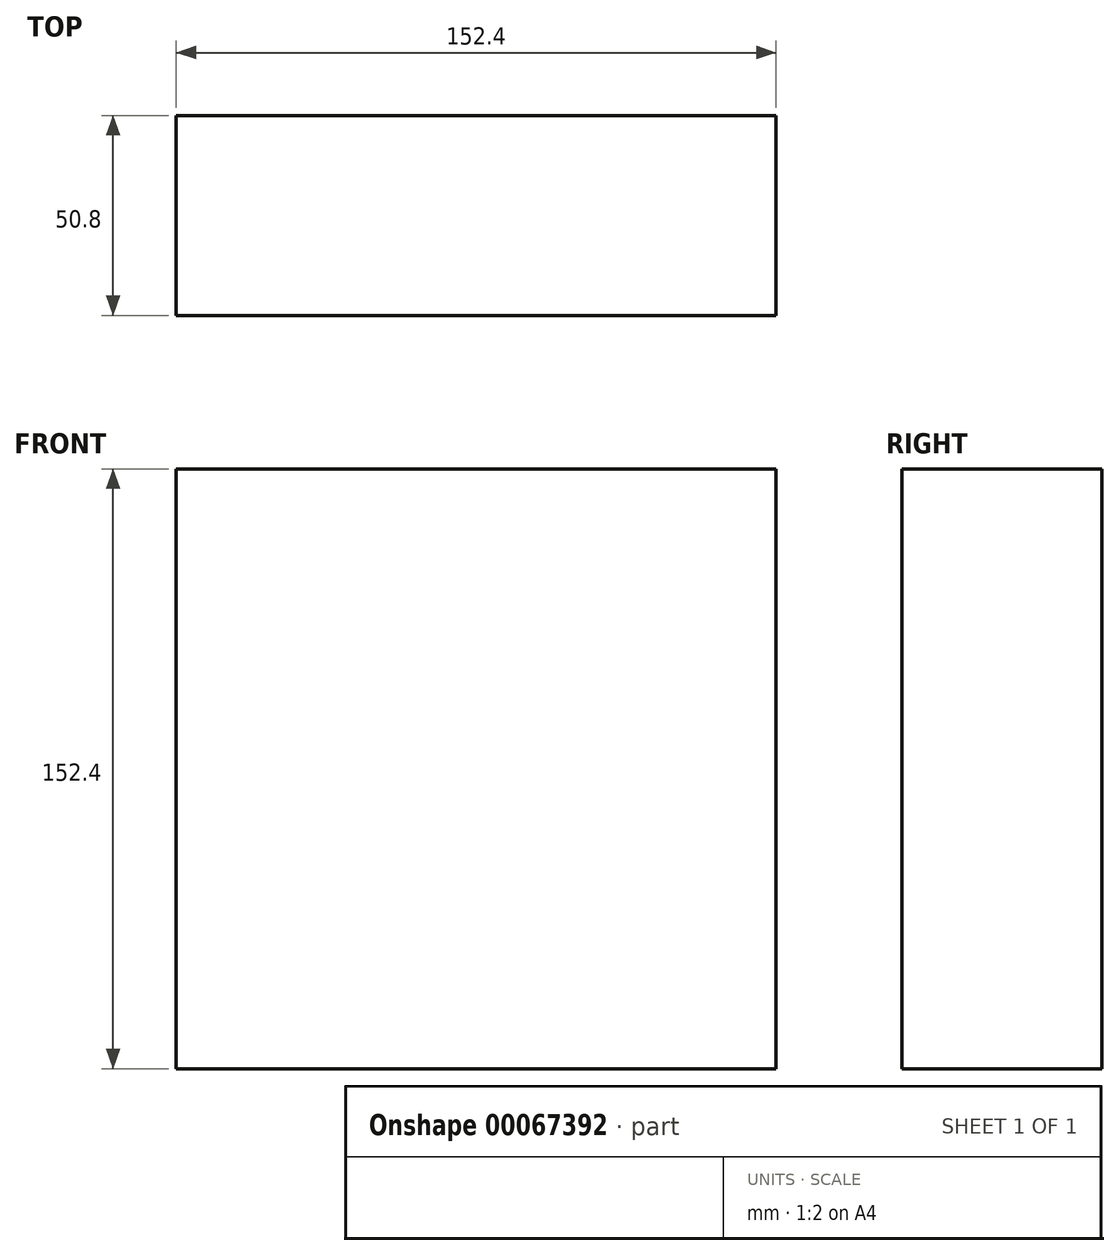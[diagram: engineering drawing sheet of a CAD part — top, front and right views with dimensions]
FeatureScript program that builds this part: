
annotation { "Feature Type Name" : "Feature", "Feature Type Description" : "" }
export const myFeature = defineFeature(function(context is Context, id is Id, definition is map)
    precondition{}
    {
        {
            var Q0;
            Q0=qCreatedBy(makeId("Front.planeOp"),FACE);
            var sketch = newSketch(context, id + "F0", { "sketchPlane" : qUnion([Q0])});
            skLineSegment(sketch, "E0.rect.bottom", {"start": v(76.2, -76.2) * mm, "end": v(-76.2, -76.2) * mm});
            skLineSegment(sketch, "E0.rect.top", {"start": v(76.2, 76.2) * mm, "end": v(-76.2, 76.2) * mm});
            skLineSegment(sketch, "E0.rect.left", {"start": v(76.2, -76.2) * mm, "end": v(76.2, 76.2) * mm});
            skLineSegment(sketch, "E0.rect.right", {"start": v(-76.2, -76.2) * mm, "end": v(-76.2, 76.2) * mm});
            skPoint(sketch, "E0.rect.middle", {"position": v(0, 0) * mm});
            skSolve(sketch);
        }
        {
            var Q0;
            Q0 = qSketchRegion(id + "F0", true);
            extrude(context, id + "F1", {"entities" : qUnion([Q0]), "endBound" : BoundingType.SYMMETRIC, "depth" : 50.8 * mm});
        }
    });
